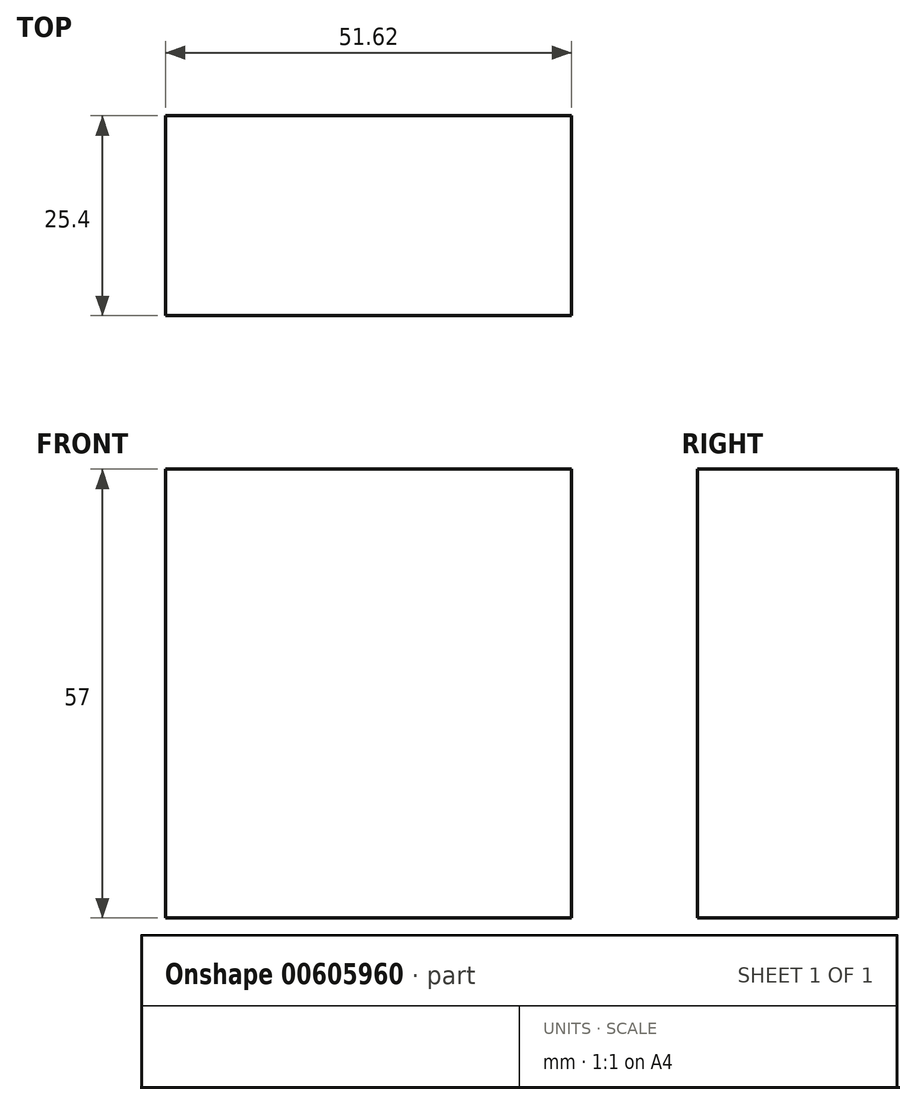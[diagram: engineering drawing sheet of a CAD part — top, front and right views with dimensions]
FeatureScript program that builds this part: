
annotation { "Feature Type Name" : "Feature", "Feature Type Description" : "" }
export const myFeature = defineFeature(function(context is Context, id is Id, definition is map)
    precondition{}
    {
        {
            var Q0;
            Q0=qCreatedBy(makeId("Front.planeOp"),FACE);
            var sketch = newSketch(context, id + "F0", { "sketchPlane" : qUnion([Q0])});
            skLineSegment(sketch, "E0.bottom", {"start": v(0, 7.67) * mm, "end": v(51.62, 7.67) * mm});
            skLineSegment(sketch, "E0.top", {"start": v(0, 64.67) * mm, "end": v(51.62, 64.67) * mm});
            skLineSegment(sketch, "E0.left", {"start": v(0, 7.67) * mm, "end": v(0, 64.67) * mm});
            skLineSegment(sketch, "E0.right", {"start": v(51.62, 7.67) * mm, "end": v(51.62, 64.67) * mm});
            skPoint(sketch, "E0.middle", {"position": v(25.8, 36.17) * mm});
            skSolve(sketch);
        }
        {
            var Q0;
            Q0 = qSketchRegion(id + "F0", true);
            extrude(context, id + "F1", {"entities" : qUnion([Q0]), "depth" : 25.4 * mm, "offsetDistance" : 25.4 * mm});
        }
    });
